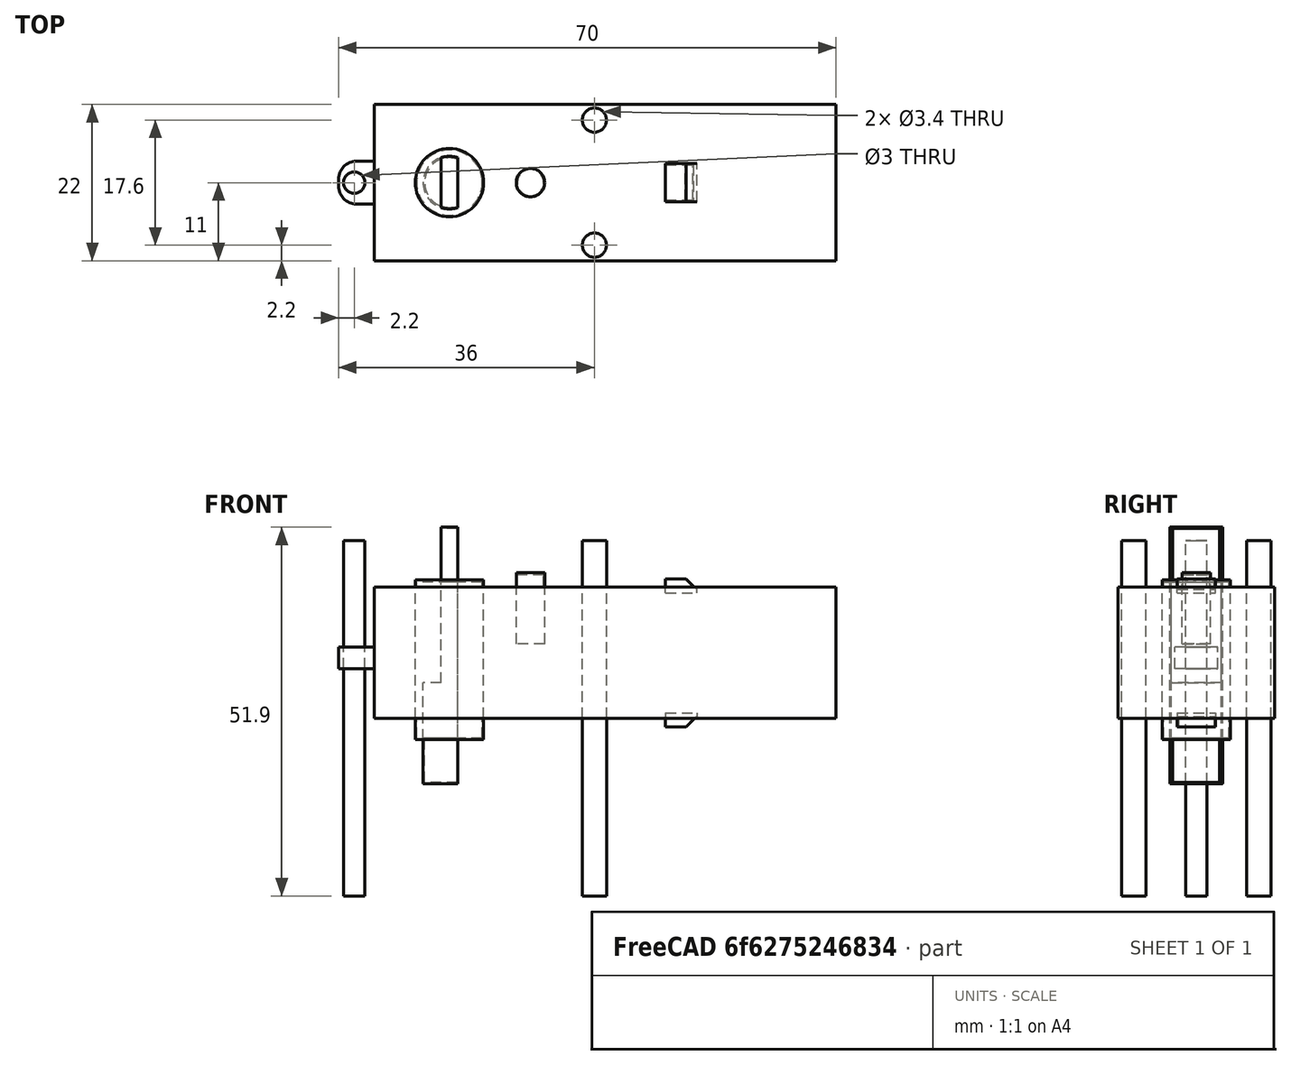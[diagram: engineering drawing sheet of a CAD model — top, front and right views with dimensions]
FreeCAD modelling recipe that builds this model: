
FCSTD DOCUMENT  (FreeCAD 0.16R6703 (Git))
Label: robosapien-motor
License: All rights reserved
LicenseURL: http://en.wikipedia.org/wiki/All_rights_reserved
objects: Part::Cylinder×12, Part::Box×10, Part::Cut×7, Part::Fuse×7, Part::Chamfer×4, Part::Fillet×2, Part::Mirroring×2, App::DocumentObjectGroup×1
note: 44 computed .brp shape members not serialized (recipe doc carries the construction recipe); baked Part::Feature solids carry a one-line shape summary decoded from their .brp

FEATURE [Part::Box] Box  label="Cube"
  Height = 18.5
  Length = 65
  Placement = pos=(0,-11,0) rot=(0,0,1;0rad)
  Width = 22
FEATURE [Part::Box] Box001  label="Cube001"
  Height = 3
  Length = 10
  Placement = pos=(-5,-3,7) rot=(0,0,1;0rad)
  Width = 6
FEATURE [Part::Cylinder] Cylinder
  Angle = 360
  Height = 10
  Placement = pos=(-2.8,0,3) rot=(0,0,1;0rad)
  Radius = 1.5
FEATURE [Part::Cut] Cut
  Base = -> Box001
  Tool = -> Cylinder
FEATURE [Part::Fillet] Fillet
  Base = -> Cut
  Edges = 1 edges r=2.5: [Edge1]
FEATURE [Part::Fillet] Fillet001
  Base = -> Fillet
  Edges = 1 edges r=2.5: [Edge3]
FEATURE [Part::Cylinder] Cylinder001  label="endhole"
  Angle = 360
  Height = 50
  Placement = pos=(-13.4,0,-25) rot=(0,0,1;0rad)
  Radius = 1.5
FEATURE [Part::Fuse] Fusion
  Base = -> Box
  Tool = -> Fillet001
FEATURE [Part::Cylinder] Cylinder002  label="Cylinder001"
  Angle = 360
  Height = 50
  Placement = pos=(31,8.8,-25) rot=(0,0,1;0rad)
  Radius = 1.7
FEATURE [Part::Cylinder] Cylinder003  label="Cylinder002"
  Angle = 360
  Height = 50
  Placement = pos=(31,-8.8,-25) rot=(0,0,1;0rad)
  Radius = 1.7
FEATURE [Part::Cylinder] Cylinder004  label="body-hole-1"
  Angle = 360
  Height = 50
  Placement = pos=(20.4,8.8,-25) rot=(0,0,1;0rad)
  Radius = 1.7
FEATURE [Part::Cylinder] Cylinder005  label="body-hole-2"
  Angle = 360
  Height = 50
  Placement = pos=(20.4,-8.8,-25) rot=(0,0,1;0rad)
  Radius = 1.7
FEATURE [Part::Cut] Cut001
  Base = -> Fusion
  Tool = -> Cylinder002
FEATURE [Part::Cut] Cut002
  Base = -> Cut001
  Tool = -> Cylinder003
FEATURE [Part::Cylinder] Cylinder006  label="Cylinder003"
  Angle = 360
  Height = 10
  Placement = pos=(22,0,10.2) rot=(0,0,1;0rad)
  Radius = 1.85
FEATURE [Part::Cylinder] Cylinder007  label="central-bump"
  Angle = 360
  Height = 10
  Placement = pos=(11.4,0,10.5) rot=(0,0,1;0rad)
  Radius = 2
FEATURE [Part::Fuse] Fusion001
  Base = -> Cut002
  Tool = -> Cylinder006
FEATURE [Part::Cylinder] Cylinder008  label="Cylinder004"
  Angle = 360
  Height = 22
  Placement = pos=(10.6,0,-2.8) rot=(0,0,1;0rad)
  Radius = 4.6
FEATURE [Part::Cylinder] Cylinder009  label="motor-boss"
  Angle = 360
  Height = 22.5
  Placement = pos=(0,0,-3) rot=(0,0,1;0rad)
  Radius = 4.8
FEATURE [Part::Fuse] Fusion002
  Base = -> Fusion001
  Tool = -> Cylinder008
FEATURE [Part::Cylinder] Cylinder010  label="motor-boss001"
  Angle = 360
  Height = 35.7
  Placement = pos=(10.6,0,-9) rot=(0,0,1;0rad)
  Radius = 3.5
FEATURE [Part::Box] Box002  label="Cube002"
  Height = 40
  Length = 10
  Placement = pos=(11.75,-5,-11) rot=(0,0,1;0rad)
  Width = 10
FEATURE [Part::Box] Box003  label="Cube003"
  Height = 40
  Length = 10
  Placement = pos=(-0.55,-5,5) rot=(0,0,1;0rad)
  Width = 10
FEATURE [Part::Cut] Cut003
  Base = -> Cylinder010
  Tool = -> Box002
FEATURE [Part::Cut] Cut004
  Base = -> Cut003
  Tool = -> Box003
FEATURE [Part::Cylinder] Cylinder011  label="motor-boss002"
  Angle = 360
  Height = 36.1
  Placement = pos=(10.6,0,-9.2) rot=(0,0,1;0rad)
  Radius = 3.7
FEATURE [Part::Box] Box004  label="Cube004"
  Height = 40
  Length = 10
  Placement = pos=(11.75,-5,-11) rot=(0,0,1;0rad)
  Width = 10
FEATURE [Part::Box] Box005  label="Cube005"
  Height = 40
  Length = 10
  Placement = pos=(-0.55,-5,5) rot=(0,0,1;0rad)
  Width = 10
FEATURE [Part::Cut] Cut005
  Base = -> Cylinder011
  Tool = -> Box004
FEATURE [Part::Cut] Cut006  label="drive"
  Base = -> Cut005
  Placement = pos=(-10.6,0,0) rot=(0,0,1;0rad)
  Tool = -> Box005
FEATURE [Part::Fuse] Fusion003
  Base = -> Fusion002
  Tool = -> Cut004
FEATURE [Part::Box] Box006  label="Cube006"
  Height = 2
  Length = 4.3
  Placement = pos=(41,-2.5,17.53) rot=(0,0,1;0rad)
  Width = 5
FEATURE [Part::Chamfer] Chamfer
  Base = -> Box006
  Edges = 1 edges r=1.5: [Edge6]
FEATURE [Part::Box] Box007  label="Cube007"
  Height = 2
  Length = 4.3
  Placement = pos=(41,-2.5,17.53) rot=(0,0,1;0rad)
  Width = 5
FEATURE [Part::Chamfer] Chamfer001
  Base = -> Box007
  Edges = 1 edges r=1.5: [Edge6]
FEATURE [Part::Mirroring] Part__Mirroring  label="Chamfer001 (Mirror #1)"
  Base = (0,0,0)
  Normal = (0,0,1)
  Placement = pos=(0,0,18.4) rot=(0,0,1;0rad)
  Source = -> Chamfer001
FEATURE [Part::Fuse] Fusion004
  Base = -> Chamfer
  Tool = -> Part__Mirroring
FEATURE [Part::Box] Box008  label="Cube008"
  Height = 2
  Length = 4.4
  Placement = pos=(41,-2.7,17.63) rot=(0,0,1;0rad)
  Width = 5.4
FEATURE [Part::Chamfer] Chamfer002
  Base = -> Box008
  Edges = 1 edges r=1.5: [Edge6]
FEATURE [Part::Box] Box009  label="Cube009"
  Height = 2
  Length = 4.4
  Placement = pos=(41,-2.7,17.63) rot=(0,0,1;0rad)
  Width = 5.4
FEATURE [Part::Chamfer] Chamfer003
  Base = -> Box009
  Edges = 1 edges r=1.5: [Edge6]
FEATURE [Part::Mirroring] Part__Mirroring001  label="Chamfer001 (Mirror #1)001"
  Base = (0,0,0)
  Normal = (0,0,1)
  Placement = pos=(0,0,18.4) rot=(0,0,1;0rad)
  Source = -> Chamfer003
FEATURE [Part::Fuse] Fusion005  label="hook-bumps"
  Base = -> Chamfer002
  Placement = pos=(-10.6,0,0) rot=(0,0,1;0rad)
  Tool = -> Part__Mirroring001
FEATURE [App::DocumentObjectGroup] Group  label="Motor-holes"
  Group = -> [Cylinder001,Cylinder005,Cylinder004,Cylinder007,Cylinder009,Cut006,Fusion005]
FEATURE [Part::Fuse] Fusion006
  Base = -> Fusion003
  Placement = pos=(-10.6,0,0) rot=(0,0,1;0rad)
  Tool = -> Fusion004
